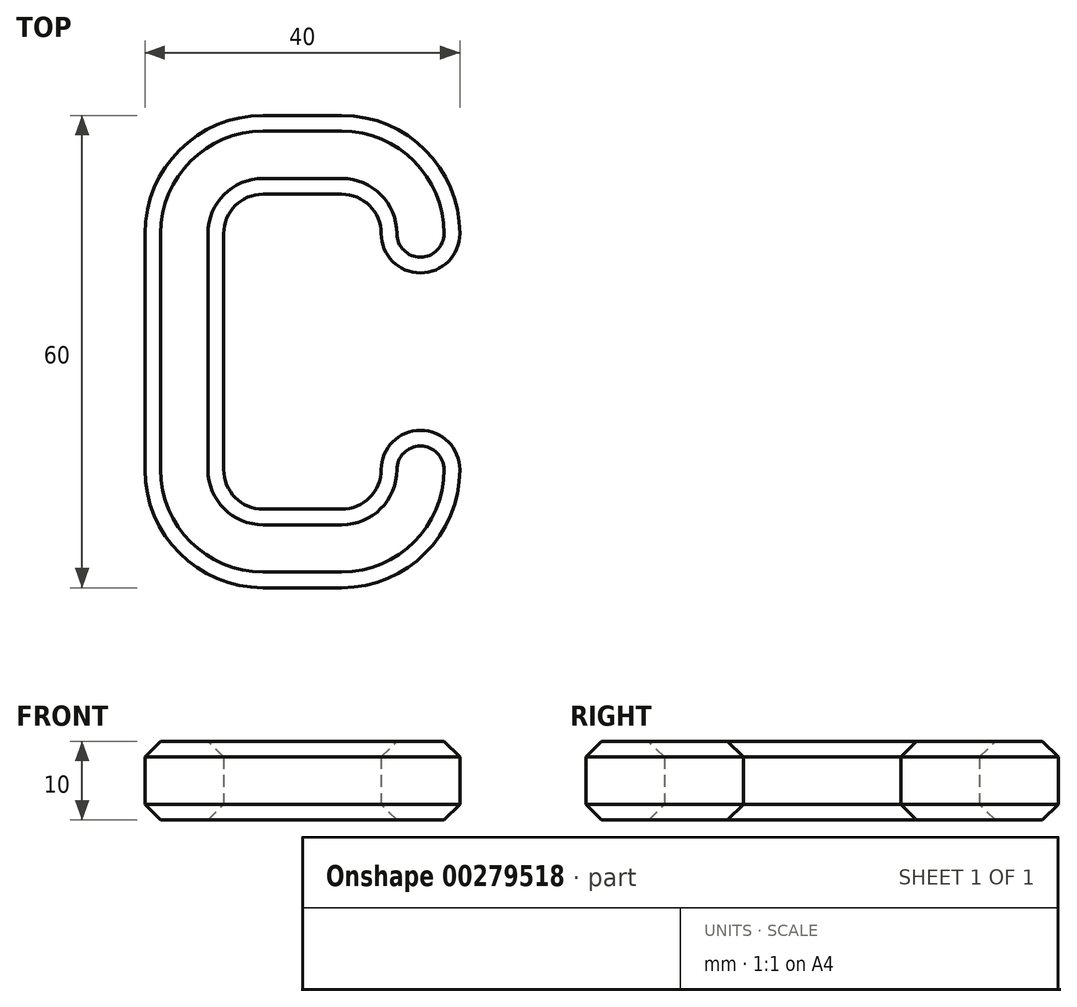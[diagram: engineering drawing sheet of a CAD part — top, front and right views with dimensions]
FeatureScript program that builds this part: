
annotation { "Feature Type Name" : "Feature", "Feature Type Description" : "" }
export const myFeature = defineFeature(function(context is Context, id is Id, definition is map)
    precondition{}
    {
        {
            var Q0;
            Q0=qCreatedBy(makeId("Top.planeOp"),FACE);
            var sketch = newSketch(context, id + "F0", { "sketchPlane" : qUnion([Q0])});
            skLineSegment(sketch, "E0.bottom", {"start": v(0, 0) * mm, "end": v(30, 0) * mm});
            skLineSegment(sketch, "E0.top", {"start": v(0, -10) * mm, "end": v(30, -10) * mm});
            skLineSegment(sketch, "E0.left", {"start": v(0, 0) * mm, "end": v(0, -10) * mm});
            skLineSegment(sketch, "E0.right", {"start": v(30, 0) * mm, "end": v(30, -10) * mm});
            skLineSegment(sketch, "E1.bottom", {"start": v(0, 40) * mm, "end": v(-10, 40) * mm});
            skLineSegment(sketch, "E1.top", {"start": v(0, -10) * mm, "end": v(-10, -10) * mm});
            skLineSegment(sketch, "E1.left", {"start": v(0, 40) * mm, "end": v(0, -10) * mm});
            skLineSegment(sketch, "E1.right", {"start": v(-10, 40) * mm, "end": v(-10, -10) * mm});
            skLineSegment(sketch, "E2.bottom", {"start": v(-10, 50) * mm, "end": v(20, 50) * mm});
            skLineSegment(sketch, "E2.top", {"start": v(-10, 40) * mm, "end": v(20, 40) * mm});
            skLineSegment(sketch, "E2.left", {"start": v(-10, 50) * mm, "end": v(-10, 40) * mm});
            skLineSegment(sketch, "E2.right", {"start": v(20, 50) * mm, "end": v(20, 40) * mm});
            skLineSegment(sketch, "E3.bottom", {"start": v(20, 50) * mm, "end": v(30, 50) * mm});
            skLineSegment(sketch, "E3.top", {"start": v(20, 30) * mm, "end": v(30, 30) * mm});
            skLineSegment(sketch, "E3.left", {"start": v(20, 50) * mm, "end": v(20, 30) * mm});
            skLineSegment(sketch, "E3.right", {"start": v(30, 50) * mm, "end": v(30, 30) * mm});
            skLineSegment(sketch, "E4.bottom", {"start": v(20, 10) * mm, "end": v(30, 10) * mm});
            skLineSegment(sketch, "E4.top", {"start": v(20, 0) * mm, "end": v(30, 0) * mm});
            skLineSegment(sketch, "E4.left", {"start": v(20, 10) * mm, "end": v(20, 0) * mm});
            skLineSegment(sketch, "E4.right", {"start": v(30, 10) * mm, "end": v(30, 0) * mm});
            skSolve(sketch);
        }
        {
            var Q0;
            {var subQ3=sQuery(id+"F0.wireOp",EDGE,"E3.bottom");Q0=makeQuery(id+"F0.imprint","IMPRINT",FACE,{"disambiguationData":[TD([[makeQuery(id+"F0.imprint","IMPRINT",EDGE,{"derivedFrom":subQ3}),-1.0]])]});}
            var Q1;
            {var subQ5=sQuery(id+"F0.wireOp",EDGE,"E2.bottom");Q1=makeQuery(id+"F0.imprint","IMPRINT",FACE,{"disambiguationData":[TD([[makeQuery(id+"F0.imprint","IMPRINT",EDGE,{"derivedFrom":subQ5}),-1.0]])]});}
            var Q2;
            {var subQ3=sQuery(id+"F0.wireOp",EDGE,"E1.top");Q2=makeQuery(id+"F0.imprint","IMPRINT",FACE,{"disambiguationData":[TD([[makeQuery(id+"F0.imprint","IMPRINT",EDGE,{"derivedFrom":subQ3}),-1.0]])]});}
            var Q3;
            {var subQ1=sQuery(id+"F0.wireOp",EDGE,"E0.bottom");Q3=makeQuery(id+"F0.imprint","IMPRINT",FACE,{"disambiguationData":[TD([[makeQuery(id+"F0.imprint","IMPRINT",EDGE,{"derivedFrom":subQ1}),-1.0]])]});}
            var Q4;
            Q4=makeQuery(id+"F0.imprint","IMPRINT",FACE,{"disambiguationData":[TD([[makeQuery(id+"F0.imprint","IMPRINT",EDGE,{"derivedFrom":sQuery(id+"F0.wireOp",EDGE,"E4.bottom")}),-1.0]])]});
            extrude(context, id + "F1", {"entities" : qUnion([Q0, Q1, Q2, Q3, Q4]), "depth" : 10 * mm});
        }
        {
            var Q0;
            Q0=makeQuery(id+"F1.opExtrude","SWEPT_EDGE",EDGE,{"disambiguationData":[OSD([sQuery(id+"F0.wireOp",EDGE,"E1.left"),sQuery(id+"F0.wireOp",EDGE,"E2.top")])]});
            var Q1;
            Q1=makeQuery(id+"F1.opExtrude","SWEPT_EDGE",EDGE,{"disambiguationData":[OSD([sQuery(id+"F0.wireOp",EDGE,"E3.top"),sQuery(id+"F0.wireOp",EDGE,"E3.left")])]});
            var Q2;
            Q2=makeQuery(id+"F1.opExtrude","SWEPT_EDGE",EDGE,{"disambiguationData":[OSD([sQuery(id+"F0.wireOp",EDGE,"E3.top"),sQuery(id+"F0.wireOp",EDGE,"E3.right")])]});
            var Q3;
            Q3=makeQuery(id+"F1.opExtrude","SWEPT_EDGE",EDGE,{"disambiguationData":[OSD([sQuery(id+"F0.wireOp",EDGE,"E0.bottom"),sQuery(id+"F0.wireOp",EDGE,"E1.left")])]});
            var Q4;
            Q4=makeQuery(id+"F1.opExtrude","SWEPT_EDGE",EDGE,{"disambiguationData":[OSD([sQuery(id+"F0.wireOp",EDGE,"E4.bottom"),sQuery(id+"F0.wireOp",EDGE,"E4.left")])]});
            var Q5;
            Q5=makeQuery(id+"F1.opExtrude","SWEPT_EDGE",EDGE,{"disambiguationData":[OSD([sQuery(id+"F0.wireOp",EDGE,"E4.bottom"),sQuery(id+"F0.wireOp",EDGE,"E4.right")])]});
            var Q6;
            Q6=makeQuery(id+"F1.opExtrude","SWEPT_EDGE",EDGE,{"disambiguationData":[OSD([sQuery(id+"F0.wireOp",EDGE,"E2.top"),sQuery(id+"F0.wireOp",EDGE,"E3.left")])]});
            var Q7;
            Q7=makeQuery(id+"F1.opExtrude","SWEPT_EDGE",EDGE,{"disambiguationData":[OSD([sQuery(id+"F0.wireOp",EDGE,"E0.bottom"),sQuery(id+"F0.wireOp",EDGE,"E4.top"),sQuery(id+"F0.wireOp",EDGE,"E4.left")])]});
            fillet(context, id + "F2", {"entities" : qUnion([Q0, Q1, Q2, Q3, Q4, Q5, Q6, Q7]), "radius" : 5 * mm, "tangentPropagation" : true, "allowEdgeOverflow" : false});
        }
        {
            var Q0;
            Q0=makeQuery(id+"F1.opExtrude","SWEPT_EDGE",EDGE,{"disambiguationData":[OSD([sQuery(id+"F0.wireOp",EDGE,"E2.bottom"),sQuery(id+"F0.wireOp",EDGE,"E2.left")])]});
            var Q1;
            Q1=makeQuery(id+"F1.opExtrude","SWEPT_EDGE",EDGE,{"disambiguationData":[OSD([sQuery(id+"F0.wireOp",EDGE,"E3.bottom"),sQuery(id+"F0.wireOp",EDGE,"E3.right")])]});
            var Q2;
            Q2=makeQuery(id+"F1.opExtrude","SWEPT_EDGE",EDGE,{"disambiguationData":[OSD([sQuery(id+"F0.wireOp",EDGE,"E0.top"),sQuery(id+"F0.wireOp",EDGE,"E0.right")])]});
            var Q3;
            Q3=makeQuery(id+"F1.opExtrude","SWEPT_EDGE",EDGE,{"disambiguationData":[OSD([sQuery(id+"F0.wireOp",EDGE,"E1.top"),sQuery(id+"F0.wireOp",EDGE,"E1.right")])]});
            fillet(context, id + "F3", {"entities" : qUnion([Q0, Q1, Q2, Q3]), "radius" : 15 * mm, "tangentPropagation" : true, "allowEdgeOverflow" : false});
        }
        {
            var Q0;
            Q0=makeQuery(id+"F1.opExtrude","CAP_EDGE",EDGE,{"disambiguationData":[OSD([sQuery(id+"F0.wireOp",EDGE,"E2.bottom"),sQuery(id+"F0.wireOp",EDGE,"E3.bottom")])],"isStart":false});
            var Q1;
            Q1=makeQuery(id+"F1.opExtrude","CAP_EDGE",EDGE,{"disambiguationData":[OSD([sQuery(id+"F0.wireOp",EDGE,"E2.bottom"),sQuery(id+"F0.wireOp",EDGE,"E3.bottom")])],"isStart":true});
            chamfer(context, id + "F4", {"entities" : qUnion([Q0, Q1]), "width" : 2 * mm, "tangentPropagation" : true});
        }
    });
